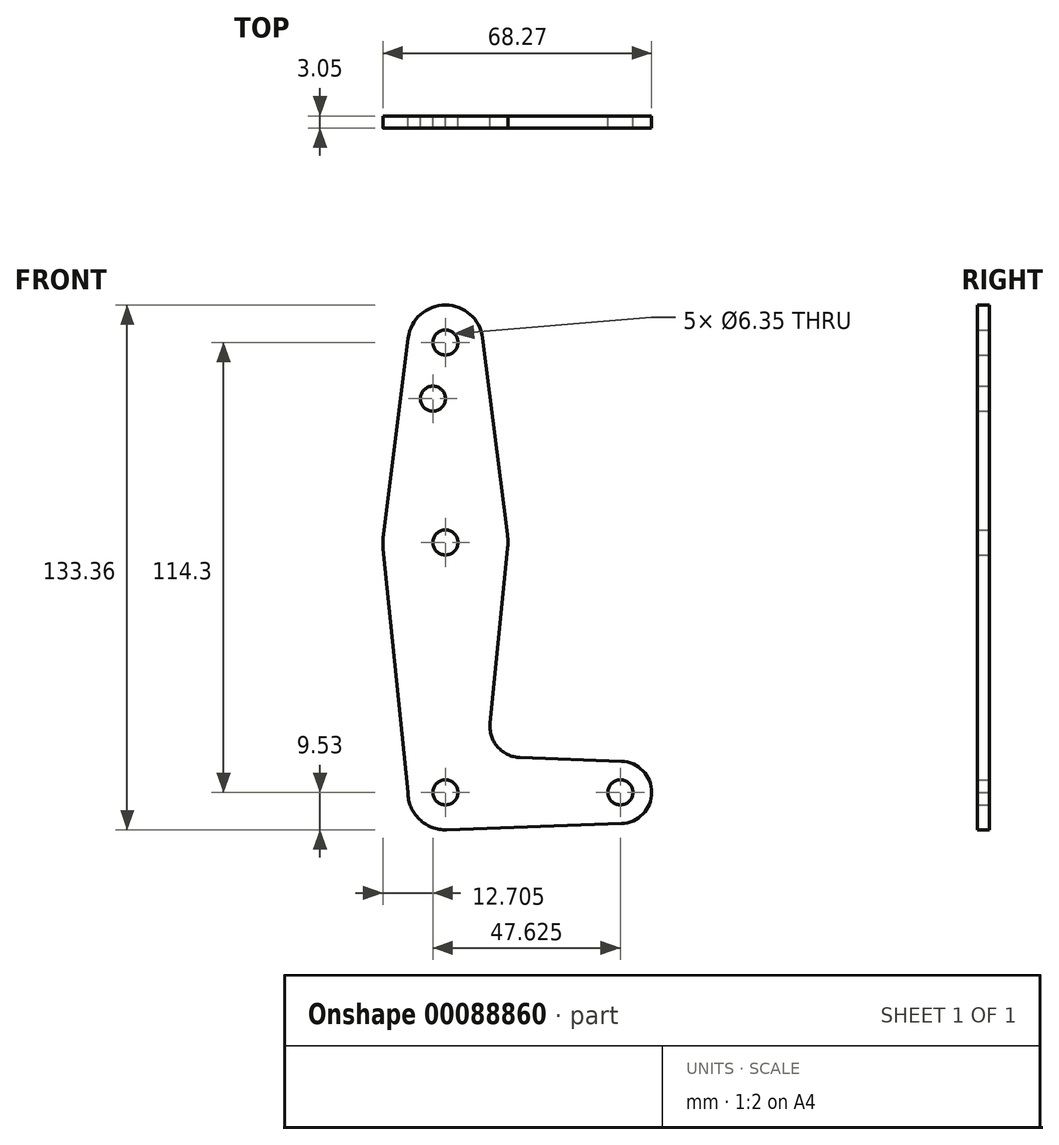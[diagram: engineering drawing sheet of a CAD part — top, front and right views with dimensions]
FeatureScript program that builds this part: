
annotation { "Feature Type Name" : "Feature", "Feature Type Description" : "" }
export const myFeature = defineFeature(function(context is Context, id is Id, definition is map)
    precondition{}
    {
        {
            var Q0;
            Q0=qCreatedBy(makeId("Front.planeOp"),FACE);
            var sketch = newSketch(context, id + "F0", { "sketchPlane" : qUnion([Q0])});
            skLineSegment(sketch, "E0", {"start": v(0, 114.3) * mm, "end": v(0, 0) * mm, "construction": true});
            skLineSegment(sketch, "E1", {"start": v(0, 0) * mm, "end": v(44.45, 0) * mm, "construction": true});
            skCircle(sketch, "E2", {"center": v(0, 114.3) * mm, "radius": 9.53 * mm});
            skCircle(sketch, "E3", {"center": v(0, 63.5) * mm, "radius": 15.88 * mm});
            skCircle(sketch, "E4", {"center": v(0, 0) * mm, "radius": 9.53 * mm});
            skCircle(sketch, "E5", {"center": v(44.45, 0) * mm, "radius": 7.94 * mm});
            skLineSegment(sketch, "E6", {"start": v(-15.8, 61.9) * mm, "end": v(-9.52, 0) * mm});
            skLineSegment(sketch, "E7", {"start": v(-15.75, 65.48) * mm, "end": v(-9.45, 115.5) * mm});
            skLineSegment(sketch, "E8", {"start": v(9.45, 115.5) * mm, "end": v(15.75, 65.48) * mm});
            skLineSegment(sketch, "E9", {"start": v(15.8, 61.91) * mm, "end": v(11.34, 17.6) * mm});
            skLineSegment(sketch, "E10", {"start": v(18.97, 8.85) * mm, "end": v(44.73, 7.93) * mm});
            skCircle(sketch, "E11", {"center": v(-3.18, 100.03) * mm, "radius": 3.18 * mm});
            skCircle(sketch, "E12", {"center": v(0, 63.5) * mm, "radius": 3.18 * mm});
            skCircle(sketch, "E13", {"center": v(0, 114.3) * mm, "radius": 3.18 * mm});
            skCircle(sketch, "E14", {"center": v(0, 0) * mm, "radius": 3.18 * mm});
            skCircle(sketch, "E15", {"center": v(44.45, 0) * mm, "radius": 3.18 * mm});
            skArc(sketch, "E16.filletArc", {"start": v(11.34, 17.6) * mm, "mid": v(13.26, 11.57) * mm, "end": v(18.97, 8.85) * mm});
            skLineSegment(sketch, "E17", {"start": v(0.34, -9.52) * mm, "end": v(44.73, -7.93) * mm});
            skSolve(sketch);
        }
        {
            var Q0;
            Q0 = qSketchRegion(id + "F0", true);
            extrude(context, id + "F1", {"entities" : qUnion([Q0]), "depth" : 3.05 * mm});
        }
    });
